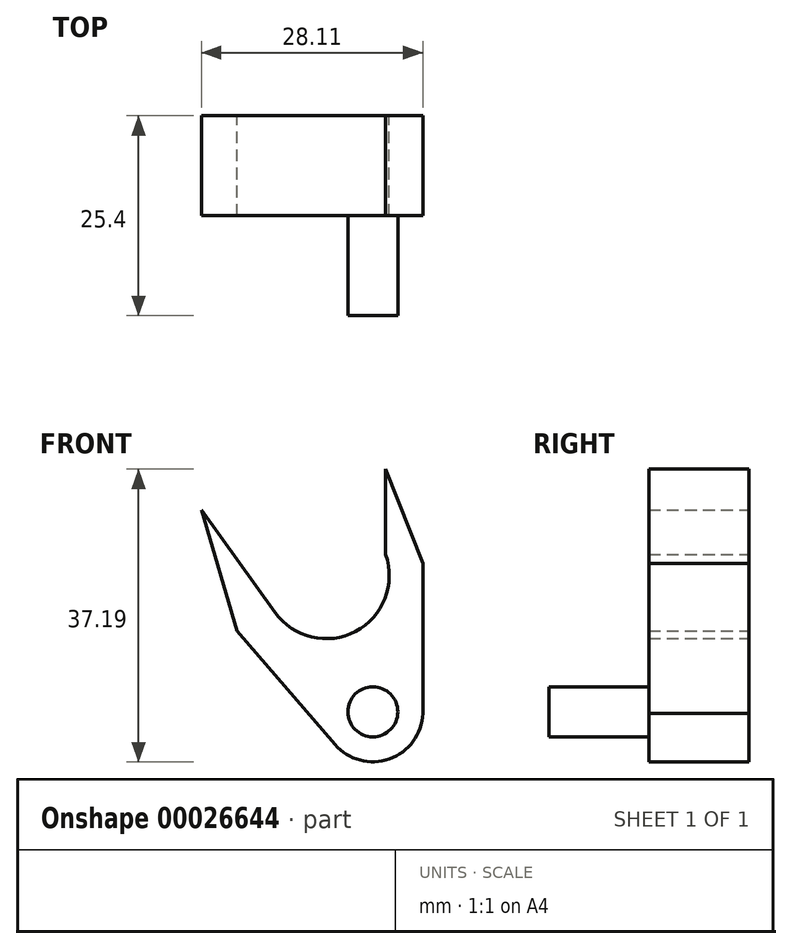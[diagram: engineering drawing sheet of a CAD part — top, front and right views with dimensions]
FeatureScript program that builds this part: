
annotation { "Feature Type Name" : "Feature", "Feature Type Description" : "" }
export const myFeature = defineFeature(function(context is Context, id is Id, definition is map)
    precondition{}
    {
        {
            var Q0;
            Q0=qCreatedBy(makeId("Front.planeOp"),FACE);
            var sketch = newSketch(context, id + "F0", { "sketchPlane" : qUnion([Q0])});
            skArc(sketch, "E0", {"start": v(-36.5, -34.98) * mm, "mid": v(-29.57, -36.82) * mm, "end": v(-25.34, -31.04) * mm});
            skLineSegment(sketch, "E1", {"start": v(-36.5, -34.98) * mm, "end": v(-48.94, -20.55) * mm});
            skLineSegment(sketch, "E2", {"start": v(-25.34, -11.99) * mm, "end": v(-25.34, -31.04) * mm});
            skLineSegment(sketch, "E3", {"start": v(-48.94, -20.55) * mm, "end": v(-53.45, -5.18) * mm});
            skLineSegment(sketch, "E4", {"start": v(-53.45, -5.18) * mm, "end": v(-44.1, -18.2) * mm});
            skLineSegment(sketch, "E5", {"start": v(-25.34, -11.99) * mm, "end": v(-30.07, 0) * mm});
            skLineSegment(sketch, "E6", {"start": v(-30.07, 0) * mm, "end": v(-30.07, -10.86) * mm});
            skArc(sketch, "E7", {"start": v(-44.1, -18.2) * mm, "mid": v(-33.89, -20.63) * mm, "end": v(-30.07, -10.86) * mm});
            skCircle(sketch, "E8", {"center": v(-31.69, -30.84) * mm, "radius": 3.18 * mm});
            skSolve(sketch);
        }
        {
            var Q0;
            Q0=makeQuery(id+"F0.imprint","IMPRINT",FACE,{"disambiguationData":[TD([[makeQuery(id+"F0.imprint","IMPRINT",EDGE,{"derivedFrom":sQuery(id+"F0.wireOp",EDGE,"E0")}),1.0]])]});
            extrude(context, id + "F1", {"entities" : qUnion([Q0]), "depth" : 12.7 * mm});
        }
        {
            var Q0;
            Q0=makeQuery(id+"F0.imprint","IMPRINT",FACE,{"disambiguationData":[TD([[makeQuery(id+"F0.imprint","IMPRINT",EDGE,{"derivedFrom":sQuery(id+"F0.wireOp",EDGE,"E8")}),1.0]])]});
            extrude(context, id + "F2", {"entities" : qUnion([Q0]), "operationType" : NewBodyOperationType.ADD, "depth" : 25.4 * mm});
        }
    });
